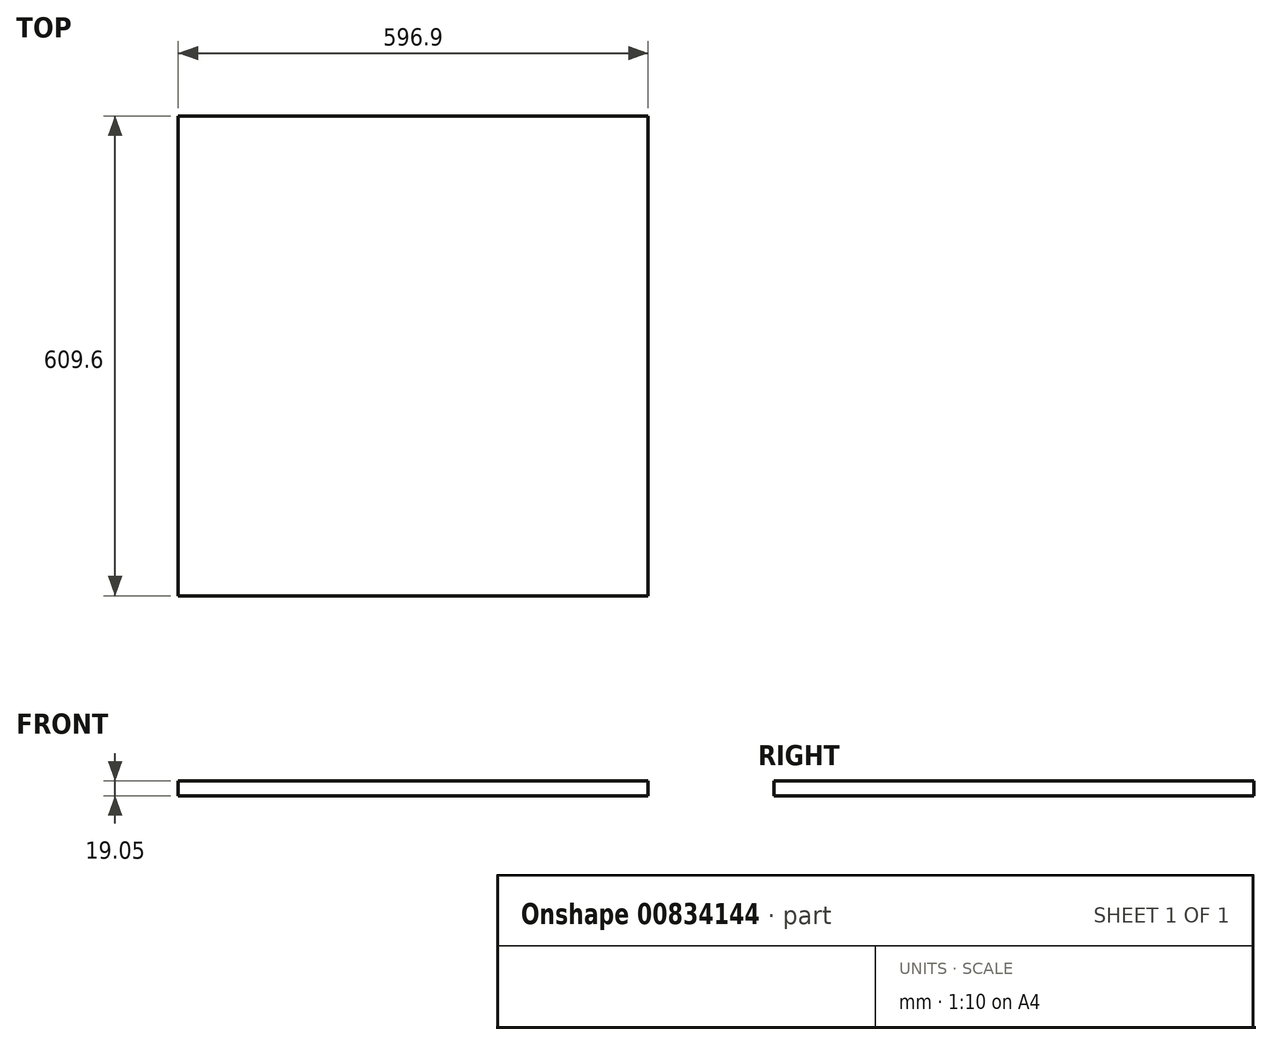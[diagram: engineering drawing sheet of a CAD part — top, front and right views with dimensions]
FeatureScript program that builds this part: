
annotation { "Feature Type Name" : "Feature", "Feature Type Description" : "" }
export const myFeature = defineFeature(function(context is Context, id is Id, definition is map)
    precondition{}
    {
        {
            var Q0;
            Q0=qCreatedBy(makeId("Top.planeOp"),FACE);
            var sketch = newSketch(context, id + "F0", { "sketchPlane" : qUnion([Q0])});
            skLineSegment(sketch, "E0.bottom", {"start": v(298.45, 0) * mm, "end": v(-298.45, 0) * mm});
            skLineSegment(sketch, "E0.top", {"start": v(298.45, -609.6) * mm, "end": v(-298.45, -609.6) * mm});
            skLineSegment(sketch, "E0.left", {"start": v(298.45, 0) * mm, "end": v(298.45, -609.6) * mm});
            skLineSegment(sketch, "E0.right", {"start": v(-298.45, 0) * mm, "end": v(-298.45, -609.6) * mm});
            skPoint(sketch, "E0.middle", {"position": v(0, -304.8) * mm});
            skSolve(sketch);
        }
        {
            var Q0;
            Q0=qSketchRegion(id+"F0",true);
            extrude(context, id + "F1", {"entities" : qUnion([Q0]), "depth" : 19.05 * mm});
        }
    });
